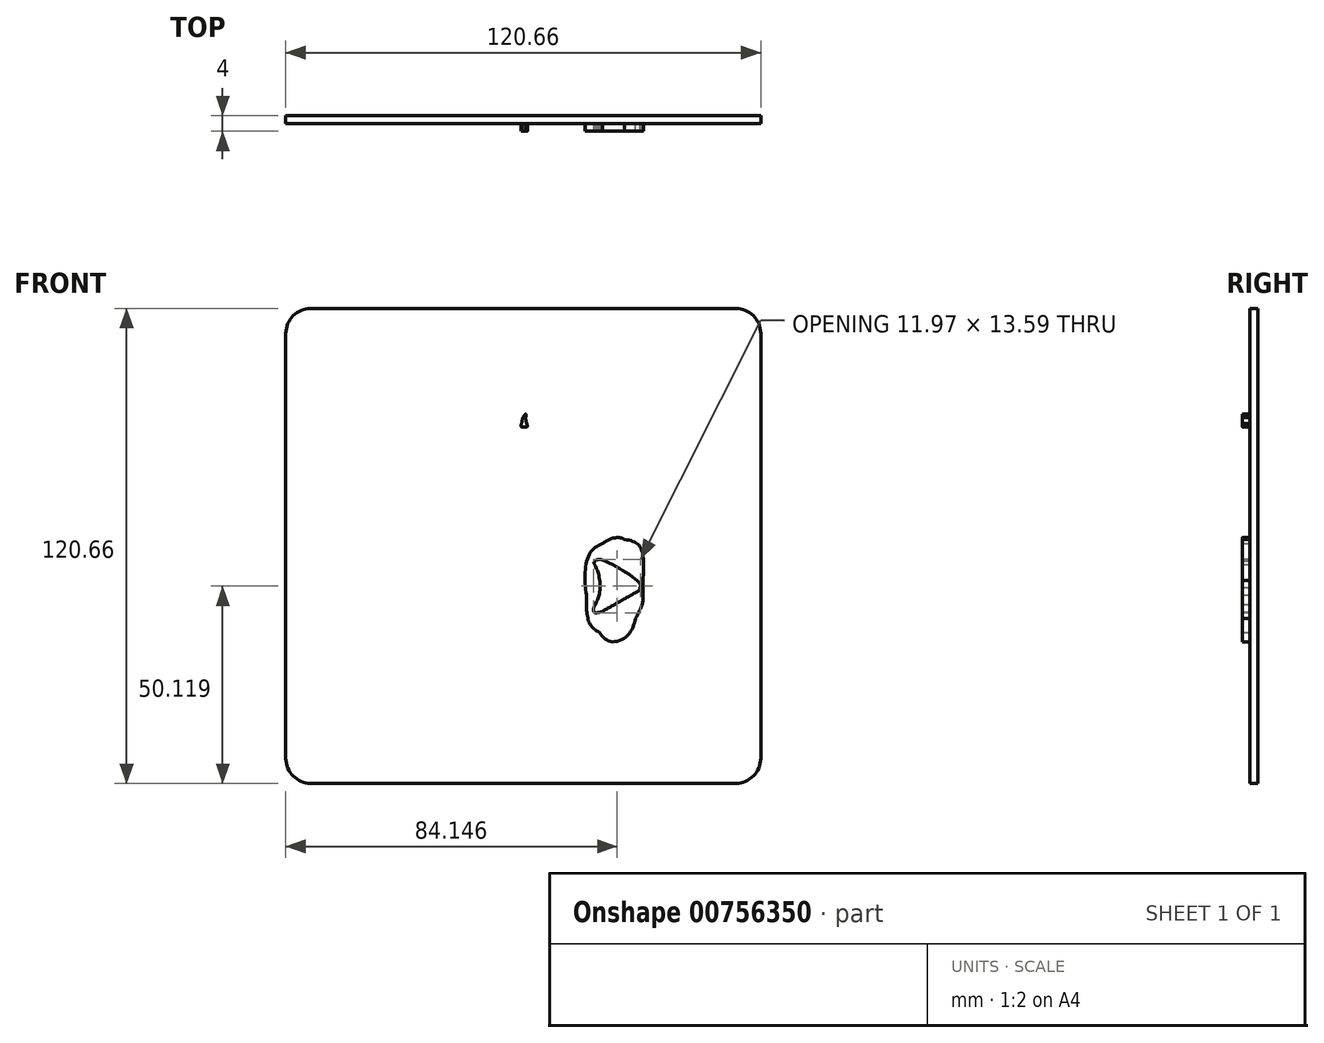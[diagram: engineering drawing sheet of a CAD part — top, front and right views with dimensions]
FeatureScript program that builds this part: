
annotation { "Feature Type Name" : "Feature", "Feature Type Description" : "" }
export const myFeature = defineFeature(function(context is Context, id is Id, definition is map)
    precondition{}
    {
        {
            var Q0;
            Q0=qCreatedBy(makeId("Front.planeOp"),FACE);
            var sketch = newSketch(context, id + "F0", { "sketchPlane" : qUnion([Q0])});
            skFitSpline(sketch, "E0", {"points": [v(-48.83, 28.95) * mm, v(-48.07, 28.98) * mm, v(-47.21, 29.05) * mm, v(-46.91, 29.12) * mm]});
            skFitSpline(sketch, "E1", {"points": [v(-46.91, 29.12) * mm, v(-46.47, 29.2) * mm, v(-46.39, 28.04) * mm, v(-46.49, 22.78) * mm]});
            skFitSpline(sketch, "E2", {"points": [v(-46.49, 22.78) * mm, v(-46.55, 19.23) * mm, v(-46.5, 15.74) * mm, v(-46.37, 15.02) * mm]});
            skFitSpline(sketch, "E3", {"points": [v(-46.37, 15.02) * mm, v(-46.15, 13.83) * mm, v(-46, 13.7) * mm, v(-44.71, 13.7) * mm]});
            skFitSpline(sketch, "E4", {"points": [v(-44.71, 13.7) * mm, v(-42.65, 13.7) * mm, v(-37.56, 14.57) * mm, v(-37.1, 15) * mm]});
            skFitSpline(sketch, "E5", {"points": [v(-37.1, 15) * mm, v(-36.86, 15.2) * mm, v(-36.6, 18.73) * mm, v(-36.49, 23.1) * mm]});
            skLineSegment(sketch, "E6", {"start": v(-50.2, -10.95) * mm, "end": v(-50.2, 28.9) * mm});
            skLineSegment(sketch, "E7", {"start": v(-50.2, 28.9) * mm, "end": v(-48.83, 28.95) * mm});
            skFitSpline(sketch, "E8", {"points": [v(-34.68, 30.97) * mm, v(-33.8, 31.05) * mm, v(-32.84, 31.3) * mm, v(-32.56, 31.53) * mm]});
            skFitSpline(sketch, "E9", {"points": [v(-32.56, 31.53) * mm, v(-31.85, 32.12) * mm, v(-31.85, 39.75) * mm, v(-32.56, 40.02) * mm]});
            skFitSpline(sketch, "E10", {"points": [v(-32.56, 40.02) * mm, v(-33.28, 40.3) * mm, v(-49.16, 37.86) * mm, v(-49.32, 37.44) * mm]});
            skFitSpline(sketch, "E11", {"points": [v(-49.32, 37.44) * mm, v(-49.4, 37.25) * mm, v(-49.62, 37.1) * mm, v(-49.83, 37.1) * mm]});
            skFitSpline(sketch, "E12", {"points": [v(-49.83, 37.1) * mm, v(-50.04, 37.1) * mm, v(-50.2, 40.06) * mm, v(-50.2, 43.95) * mm]});
            skLineSegment(sketch, "E13", {"start": v(-36.49, 23.1) * mm, "end": v(-36.29, 30.84) * mm});
            skLineSegment(sketch, "E14", {"start": v(-36.29, 30.84) * mm, "end": v(-34.68, 30.97) * mm});
            skFitSpline(sketch, "E15", {"points": [v(-5.95, 50.75) * mm, v(18.57, 50.73) * mm, v(37.58, 50.56) * mm, v(36.69, 50.37) * mm]});
            skFitSpline(sketch, "E16", {"points": [v(36.69, 50.37) * mm, v(35.8, 50.2) * mm, v(34.4, 50.03) * mm, v(33.6, 50.02) * mm]});
            skFitSpline(sketch, "E17", {"points": [v(33.6, 50.02) * mm, v(31.95, 50) * mm, v(32.14, 50.38) * mm, v(30.21, 43.14) * mm]});
            skFitSpline(sketch, "E18", {"points": [v(30.21, 43.14) * mm, v(29.35, 39.9) * mm, v(29.01, 39.48) * mm, v(28.67, 41.2) * mm]});
            skFitSpline(sketch, "E19", {"points": [v(28.67, 41.2) * mm, v(27.94, 44.86) * mm, v(26.68, 48.75) * mm, v(26.15, 48.95) * mm]});
            skFitSpline(sketch, "E20", {"points": [v(26.15, 48.95) * mm, v(25.39, 49.24) * mm, v(17.91, 48.05) * mm, v(17.3, 47.54) * mm]});
            skFitSpline(sketch, "E21", {"points": [v(17.3, 47.54) * mm, v(17.05, 47.33) * mm, v(16.06, 42.3) * mm, v(15.12, 36.38) * mm]});
            skFitSpline(sketch, "E22", {"points": [v(15.12, 36.38) * mm, v(14.17, 30.45) * mm, v(13.28, 25.47) * mm, v(13.13, 25.3) * mm]});
            skFitSpline(sketch, "E23", {"points": [v(13.13, 25.3) * mm, v(12.99, 25.14) * mm, v(11.26, 29.5) * mm, v(9.3, 34.98) * mm]});
            skFitSpline(sketch, "E24", {"points": [v(9.3, 34.98) * mm, v(7.34, 40.46) * mm, v(5.52, 45.19) * mm, v(5.26, 45.47) * mm]});
            skFitSpline(sketch, "E25", {"points": [v(5.26, 45.47) * mm, v(4.88, 45.88) * mm, v(3.92, 45.85) * mm, v(0.24, 45.3) * mm]});
            skFitSpline(sketch, "E26", {"points": [v(0.24, 45.3) * mm, v(-3.47, 44.73) * mm, v(-4.41, 44.45) * mm, v(-4.84, 43.77) * mm]});
            skFitSpline(sketch, "E27", {"points": [v(-4.84, 43.77) * mm, v(-5.13, 43.31) * mm, v(-7.06, 37.79) * mm, v(-9.14, 31.5) * mm]});
            skLineSegment(sketch, "E28", {"start": v(-50.2, 43.95) * mm, "end": v(-50.2, 50.8) * mm});
            skLineSegment(sketch, "E29", {"start": v(-50.2, 50.8) * mm, "end": v(-5.95, 50.75) * mm});
            skFitSpline(sketch, "E30", {"points": [v(-15.12, 25.6) * mm, v(-16.12, 25.6) * mm, v(-17.71, 25.47) * mm, v(-18.67, 25.33) * mm]});
            skFitSpline(sketch, "E31", {"points": [v(-18.67, 25.33) * mm, v(-19.9, 25.14) * mm, v(-20.36, 25.2) * mm, v(-20.25, 25.53) * mm]});
            skFitSpline(sketch, "E32", {"points": [v(-20.25, 25.53) * mm, v(-20.16, 25.79) * mm, v(-18.93, 26.19) * mm, v(-17.5, 26.42) * mm]});
            skFitSpline(sketch, "E33", {"points": [v(-17.5, 26.42) * mm, v(-16.07, 26.66) * mm, v(-14.68, 26.99) * mm, v(-14.4, 27.16) * mm]});
            skFitSpline(sketch, "E34", {"points": [v(-14.4, 27.16) * mm, v(-14.08, 27.36) * mm, v(-13.9, 28.56) * mm, v(-13.9, 30.68) * mm]});
            skFitSpline(sketch, "E35", {"points": [v(-13.9, 30.68) * mm, v(-13.9, 34.47) * mm, v(-14, 34.55) * mm, v(-17.61, 33.92) * mm]});
            skFitSpline(sketch, "E36", {"points": [v(-17.61, 33.92) * mm, v(-19.93, 33.5) * mm, v(-20.8, 33.56) * mm, v(-20.28, 34.08) * mm]});
            skFitSpline(sketch, "E37", {"points": [v(-20.28, 34.08) * mm, v(-20.17, 34.2) * mm, v(-18.68, 34.53) * mm, v(-16.98, 34.83) * mm]});
            skFitSpline(sketch, "E38", {"points": [v(-16.98, 34.83) * mm, v(-15.28, 35.13) * mm, v(-13.76, 35.5) * mm, v(-13.6, 35.66) * mm]});
            skFitSpline(sketch, "E39", {"points": [v(-13.6, 35.66) * mm, v(-13.44, 35.82) * mm, v(-13.24, 37.35) * mm, v(-13.17, 39.06) * mm]});
            skFitSpline(sketch, "E40", {"points": [v(-13.17, 39.06) * mm, v(-13.06, 41.36) * mm, v(-13.17, 42.3) * mm, v(-13.59, 42.64) * mm]});
            skFitSpline(sketch, "E41", {"points": [v(-13.59, 42.64) * mm, v(-14.02, 43) * mm, v(-15.9, 42.84) * mm, v(-21.65, 41.96) * mm]});
            skFitSpline(sketch, "E42", {"points": [v(-21.65, 41.96) * mm, v(-25.78, 41.33) * mm, v(-29.35, 40.7) * mm, v(-29.6, 40.54) * mm]});
            skFitSpline(sketch, "E43", {"points": [v(-29.6, 40.54) * mm, v(-29.9, 40.36) * mm, v(-30.04, 36.55) * mm, v(-30.04, 28.39) * mm]});
            skFitSpline(sketch, "E44", {"points": [v(-30.04, 28.39) * mm, v(-30.04, 17.74) * mm, v(-29.97, 16.48) * mm, v(-29.37, 16.25) * mm]});
            skFitSpline(sketch, "E45", {"points": [v(-29.37, 16.25) * mm, v(-28.51, 15.92) * mm, v(-14.34, 18.03) * mm, v(-13.66, 18.59) * mm]});
            skFitSpline(sketch, "E46", {"points": [v(-13.66, 18.59) * mm, v(-13.38, 18.82) * mm, v(-12.8, 18.9) * mm, v(-12.37, 18.77) * mm]});
            skFitSpline(sketch, "E47", {"points": [v(-12.37, 18.77) * mm, v(-11.95, 18.64) * mm, v(-9.8, 18.81) * mm, v(-7.61, 19.16) * mm]});
            skFitSpline(sketch, "E48", {"points": [v(-7.61, 19.16) * mm, v(-3.57, 19.8) * mm, v(-2.62, 20.3) * mm, v(-2.62, 21.82) * mm]});
            skFitSpline(sketch, "E49", {"points": [v(-2.62, 21.82) * mm, v(-2.62, 22.75) * mm, v(-2.36, 22.88) * mm, v(0.38, 23.31) * mm]});
            skFitSpline(sketch, "E50", {"points": [v(0.38, 23.31) * mm, v(2.69, 23.68) * mm, v(2.7, 23.67) * mm, v(3.1, 22.56) * mm]});
            skFitSpline(sketch, "E51", {"points": [v(3.1, 22.56) * mm, v(3.3, 21.94) * mm, v(3.75, 21.33) * mm, v(4.07, 21.2) * mm]});
            skFitSpline(sketch, "E52", {"points": [v(4.07, 21.2) * mm, v(4.4, 21.08) * mm, v(6.7, 21.32) * mm, v(9.18, 21.74) * mm]});
            skFitSpline(sketch, "E53", {"points": [v(9.18, 21.74) * mm, v(11.67, 22.16) * mm, v(15.39, 22.73) * mm, v(17.44, 23) * mm]});
            skFitSpline(sketch, "E54", {"points": [v(17.44, 23) * mm, v(19.5, 23.28) * mm, v(21.45, 23.7) * mm, v(21.8, 23.96) * mm]});
            skFitSpline(sketch, "E55", {"points": [v(21.8, 23.96) * mm, v(22.24, 24.28) * mm, v(22.56, 25.7) * mm, v(22.87, 28.84) * mm]});
            skFitSpline(sketch, "E56", {"points": [v(22.87, 28.84) * mm, v(23.12, 31.27) * mm, v(23.42, 32.98) * mm, v(23.54, 32.65) * mm]});
            skFitSpline(sketch, "E57", {"points": [v(23.54, 32.65) * mm, v(23.67, 32.32) * mm, v(24.32, 30.42) * mm, v(24.99, 28.42) * mm]});
            skLineSegment(sketch, "E58", {"start": v(-9.14, 31.5) * mm, "end": v(-12.9, 20.05) * mm});
            skLineSegment(sketch, "E59", {"start": v(-12.9, 20.05) * mm, "end": v(-13.1, 22.83) * mm});
            skLineSegment(sketch, "E60", {"start": v(-13.1, 22.83) * mm, "end": v(-13.3, 25.6) * mm});
            skLineSegment(sketch, "E61", {"start": v(-13.3, 25.6) * mm, "end": v(-15.12, 25.6) * mm});
            skFitSpline(sketch, "E62", {"points": [v(28.5, 24.87) * mm, v(29.77, 24.91) * mm, v(31.14, 25.13) * mm, v(31.54, 25.34) * mm]});
            skFitSpline(sketch, "E63", {"points": [v(31.54, 25.34) * mm, v(32.03, 25.6) * mm, v(32.74, 27.31) * mm, v(33.68, 30.47) * mm]});
            skFitSpline(sketch, "E64", {"points": [v(33.68, 30.47) * mm, v(35.03, 35.05) * mm, v(35.08, 35.16) * mm, v(35.35, 33.63) * mm]});
            skFitSpline(sketch, "E65", {"points": [v(35.35, 33.63) * mm, v(35.5, 32.76) * mm, v(35.64, 31.2) * mm, v(35.66, 30.16) * mm]});
            skFitSpline(sketch, "E66", {"points": [v(35.66, 30.16) * mm, v(35.7, 27.24) * mm, v(36.23, 26.2) * mm, v(37.7, 26.2) * mm]});
            skFitSpline(sketch, "E67", {"points": [v(37.7, 26.2) * mm, v(39.94, 26.2) * mm, v(44.54, 27.12) * mm, v(44.98, 27.65) * mm]});
            skFitSpline(sketch, "E68", {"points": [v(44.98, 27.65) * mm, v(45.46, 28.22) * mm, v(42.26, 49.69) * mm, v(41.66, 49.93) * mm]});
            skFitSpline(sketch, "E69", {"points": [v(41.66, 49.93) * mm, v(41.48, 50) * mm, v(41.33, 50.23) * mm, v(41.33, 50.43) * mm]});
            skFitSpline(sketch, "E70", {"points": [v(41.33, 50.43) * mm, v(41.33, 50.63) * mm, v(43.32, 50.8) * mm, v(45.76, 50.8) * mm]});
            skLineSegment(sketch, "E71", {"start": v(24.99, 28.42) * mm, "end": v(26.2, 24.8) * mm});
            skLineSegment(sketch, "E72", {"start": v(26.2, 24.8) * mm, "end": v(28.5, 24.87) * mm});
            skFitSpline(sketch, "E73", {"points": [v(50.16, 24.3) * mm, v(50.13, 0.44) * mm, v(50.07, -1.9) * mm, v(49.57, 0.86) * mm]});
            skFitSpline(sketch, "E74", {"points": [v(49.57, 0.86) * mm, v(47.83, 10.44) * mm, v(42.68, 16.68) * mm, v(34.5, 19.1) * mm]});
            skFitSpline(sketch, "E75", {"points": [v(34.5, 19.1) * mm, v(31.35, 20.04) * mm, v(24.68, 19.96) * mm, v(20.42, 18.94) * mm]});
            skFitSpline(sketch, "E76", {"points": [v(20.42, 18.94) * mm, v(9.2, 16.25) * mm, v(0.7, 7.6) * mm, v(-2.41, -4.26) * mm]});
            skFitSpline(sketch, "E77", {"points": [v(-2.41, -4.26) * mm, v(-3.54, -8.57) * mm, v(-3.91, -13.72) * mm, v(-3.42, -18.17) * mm]});
            skFitSpline(sketch, "E78", {"points": [v(-3.42, -18.17) * mm, v(-2.1, -30.14) * mm, v(3.3, -37.33) * mm, v(12.81, -39.77) * mm]});
            skFitSpline(sketch, "E79", {"points": [v(12.81, -39.77) * mm, v(15.86, -40.56) * mm, v(22.88, -40.32) * mm, v(26.6, -39.3) * mm]});
            skFitSpline(sketch, "E80", {"points": [v(26.6, -39.3) * mm, v(30.15, -38.35) * mm, v(35.13, -35.82) * mm, v(37.89, -33.58) * mm]});
            skFitSpline(sketch, "E81", {"points": [v(37.89, -33.58) * mm, v(44.49, -28.24) * mm, v(48.28, -20.71) * mm, v(49.93, -9.68) * mm]});
            skFitSpline(sketch, "E82", {"points": [v(49.93, -9.68) * mm, v(50.02, -9.12) * mm, v(50.11, -18.15) * mm, v(50.14, -29.73) * mm]});
            skLineSegment(sketch, "E83", {"start": v(45.76, 50.8) * mm, "end": v(50.2, 50.8) * mm});
            skLineSegment(sketch, "E84", {"start": v(50.2, 50.8) * mm, "end": v(50.16, 24.3) * mm});
            skFitSpline(sketch, "E85", {"points": [v(-26.3, -46.61) * mm, v(-21.46, -45.87) * mm, v(-17.44, -45.2) * mm, v(-17.36, -45.1) * mm]});
            skFitSpline(sketch, "E86", {"points": [v(-17.36, -45.1) * mm, v(-16.98, -44.72) * mm, v(-16.64, 12) * mm, v(-17.02, 12.23) * mm]});
            skFitSpline(sketch, "E87", {"points": [v(-17.02, 12.23) * mm, v(-17.56, 12.56) * mm, v(-44.6, 8.46) * mm, v(-45.26, 7.95) * mm]});
            skFitSpline(sketch, "E88", {"points": [v(-45.26, 7.95) * mm, v(-45.63, 7.66) * mm, v(-45.76, 5.36) * mm, v(-45.76, -1.06) * mm]});
            skLineSegment(sketch, "E89", {"start": v(50.14, -29.73) * mm, "end": v(50.2, -50.8) * mm});
            skLineSegment(sketch, "E90", {"start": v(50.2, -50.8) * mm, "end": v(0, -50.8) * mm});
            skLineSegment(sketch, "E91", {"start": v(0, -50.8) * mm, "end": v(-50.2, -50.8) * mm});
            skLineSegment(sketch, "E92", {"start": v(-50.2, -50.8) * mm, "end": v(-50.2, -10.95) * mm});
            skFitSpline(sketch, "E93", {"points": [v(-44.05, -9.65) * mm, v(-43.1, -9.63) * mm, v(-41.34, -9.47) * mm, v(-40.12, -9.3) * mm]});
            skFitSpline(sketch, "E94", {"points": [v(-40.12, -9.3) * mm, v(-38.8, -9.1) * mm, v(-37.7, -9.12) * mm, v(-37.42, -9.35) * mm]});
            skFitSpline(sketch, "E95", {"points": [v(-37.42, -9.35) * mm, v(-37.06, -9.64) * mm, v(-37, -14.37) * mm, v(-37.18, -28.85) * mm]});
            skLineSegment(sketch, "E96", {"start": v(-45.76, -1.06) * mm, "end": v(-45.76, -9.68) * mm});
            skLineSegment(sketch, "E97", {"start": v(-45.76, -9.68) * mm, "end": v(-44.05, -9.65) * mm});
            skFitSpline(sketch, "E98", {"points": [v(-36.25, -47.97) * mm, v(-35.6, -47.96) * mm, v(-31.12, -47.35) * mm, v(-26.3, -46.61) * mm]});
            skLineSegment(sketch, "E99", {"start": v(-37.18, -28.85) * mm, "end": v(-37.42, -47.98) * mm});
            skLineSegment(sketch, "E100", {"start": v(-37.42, -47.98) * mm, "end": v(-36.25, -47.97) * mm});
            skFitSpline(sketch, "E101", {"points": [v(19.3, -21.98) * mm, v(17.25, -20.36) * mm, v(16.23, -17.4) * mm, v(16.01, -12.5) * mm]});
            skFitSpline(sketch, "E102", {"points": [v(16.01, -12.5) * mm, v(15.74, -6.21) * mm, v(17.29, -1.31) * mm, v(20.13, 0.55) * mm]});
            skFitSpline(sketch, "E103", {"points": [v(20.13, 0.55) * mm, v(21.76, 1.62) * mm, v(24.31, 2.1) * mm, v(25.76, 1.63) * mm]});
            skFitSpline(sketch, "E104", {"points": [v(25.76, 1.63) * mm, v(29, 0.56) * mm, v(30.45, -2.7) * mm, v(30.43, -8.83) * mm]});
            skFitSpline(sketch, "E105", {"points": [v(30.43, -8.83) * mm, v(30.42, -13.3) * mm, v(30.02, -15.37) * mm, v(28.57, -18.43) * mm]});
            skFitSpline(sketch, "E106", {"points": [v(28.57, -18.43) * mm, v(26.57, -22.66) * mm, v(22.26, -24.31) * mm, v(19.3, -21.98) * mm]});
            skFitSpline(sketch, "E107", {"points": [v(24.6, -14.09) * mm, v(28.17, -12.07) * mm, v(29.63, -11.03) * mm, v(29.63, -10.5) * mm]});
            skFitSpline(sketch, "E108", {"points": [v(29.63, -10.5) * mm, v(29.63, -9.55) * mm, v(19.47, -3.42) * mm, v(18.5, -3.79) * mm]});
            skFitSpline(sketch, "E109", {"points": [v(18.5, -3.79) * mm, v(18.1, -3.95) * mm, v(17.95, -4.29) * mm, v(18.11, -4.7) * mm]});
            skFitSpline(sketch, "E110", {"points": [v(18.11, -4.7) * mm, v(19.22, -7.59) * mm, v(19.3, -12.19) * mm, v(18.3, -14.82) * mm]});
            skFitSpline(sketch, "E111", {"points": [v(18.3, -14.82) * mm, v(17.83, -16.07) * mm, v(18.1, -16.93) * mm, v(18.95, -16.93) * mm]});
            skFitSpline(sketch, "E112", {"points": [v(18.95, -16.93) * mm, v(19.3, -16.93) * mm, v(21.84, -15.65) * mm, v(24.6, -14.09) * mm]});
            skFitSpline(sketch, "E113", {"points": [v(-0.36, 31.35) * mm, v(-0.05, 32.64) * mm, v(0.6, 33.51) * mm, v(0.61, 32.64) * mm]});
            skFitSpline(sketch, "E114", {"points": [v(0.61, 32.64) * mm, v(0.61, 32.32) * mm, v(0.73, 31.64) * mm, v(0.86, 31.15) * mm]});
            skFitSpline(sketch, "E115", {"points": [v(0.86, 31.15) * mm, v(1.06, 30.41) * mm, v(0.94, 30.24) * mm, v(0.24, 30.24) * mm]});
            skFitSpline(sketch, "E116", {"points": [v(0.24, 30.24) * mm, v(-0.5, 30.24) * mm, v(-0.58, 30.4) * mm, v(-0.36, 31.35) * mm]});
            skSolve(sketch);
        }
        {
            var Q0;
            Q0=makeQuery(id+"F0.imprint","IMPRINT",FACE,{"disambiguationData":[TD([[makeQuery(id+"F0.imprint","IMPRINT",EDGE,{"derivedFrom":sQuery(id+"F0.wireOp",EDGE,"E0")}),-1.0]])]});
            var Q1;
            Q1=makeQuery(id+"F0.imprint","IMPRINT",FACE,{"disambiguationData":[TD([[makeQuery(id+"F0.imprint","IMPRINT",EDGE,{"derivedFrom":sQuery(id+"F0.wireOp",EDGE,"E101")}),-1.0]])]});
            var Q2;
            Q2=makeQuery(id+"F0.imprint","IMPRINT",FACE,{"disambiguationData":[TD([[makeQuery(id+"F0.imprint","IMPRINT",EDGE,{"derivedFrom":sQuery(id+"F0.wireOp",EDGE,"E113")}),-1.0]])]});
            extrude(context, id + "F1", {"entities" : qUnion([Q0, Q1, Q2]), "depth" : 2 * mm, "offsetDistance" : 25.4 * mm});
        }
        {
            var Q0;
            Q0=qCreatedBy(makeId("Front.planeOp"),FACE);
            var sketch = newSketch(context, id + "F2", { "sketchPlane" : qUnion([Q0])});
            skLineSegment(sketch, "E117.bottom", {"start": v(60.33, 60.33) * mm, "end": v(-60.32, 60.33) * mm});
            skLineSegment(sketch, "E117.top", {"start": v(60.32, -60.33) * mm, "end": v(-60.33, -60.33) * mm});
            skLineSegment(sketch, "E117.left", {"start": v(60.33, 60.33) * mm, "end": v(60.32, -60.33) * mm});
            skLineSegment(sketch, "E117.right", {"start": v(-60.32, 60.33) * mm, "end": v(-60.33, -60.33) * mm});
            skPoint(sketch, "E117.middle", {"position": v(0, 0) * mm});
            skSolve(sketch);
        }
        {
            var Q0;
            Q0=makeQuery(id+"F2.imprint","IMPRINT",FACE,{"disambiguationData":[TD([[makeQuery(id+"F2.imprint","IMPRINT",EDGE,{"derivedFrom":sQuery(id+"F2.wireOp",EDGE,"E117.bottom")}),1.0]])]});
            extrude(context, id + "F3", {"entities" : qUnion([Q0]), "oppositeDirection" : true, "depth" : 2 * mm, "offsetDistance" : 25.4 * mm});
        }
        {
            var Q0;
            Q0=makeQuery(id+"F3.opExtrude","SWEPT_EDGE",EDGE,{"disambiguationData":[OSD([sQuery(id+"F2.wireOp",EDGE,"E117.bottom"),sQuery(id+"F2.wireOp",EDGE,"E117.right")])]});
            var Q1;
            Q1=makeQuery(id+"F3.opExtrude","SWEPT_EDGE",EDGE,{"disambiguationData":[OSD([sQuery(id+"F2.wireOp",EDGE,"E117.bottom"),sQuery(id+"F2.wireOp",EDGE,"E117.left")])]});
            var Q2;
            Q2=makeQuery(id+"F3.opExtrude","SWEPT_EDGE",EDGE,{"disambiguationData":[OSD([sQuery(id+"F2.wireOp",EDGE,"E117.top"),sQuery(id+"F2.wireOp",EDGE,"E117.left")])]});
            var Q3;
            Q3=makeQuery(id+"F3.opExtrude","SWEPT_EDGE",EDGE,{"disambiguationData":[OSD([sQuery(id+"F2.wireOp",EDGE,"E117.top"),sQuery(id+"F2.wireOp",EDGE,"E117.right")])]});
            fillet(context, id + "F4", {"entities" : qUnion([Q0, Q1, Q2, Q3]), "radius" : 6.35 * mm, "tangentPropagation" : true, "allowEdgeOverflow" : false});
        }
    });
